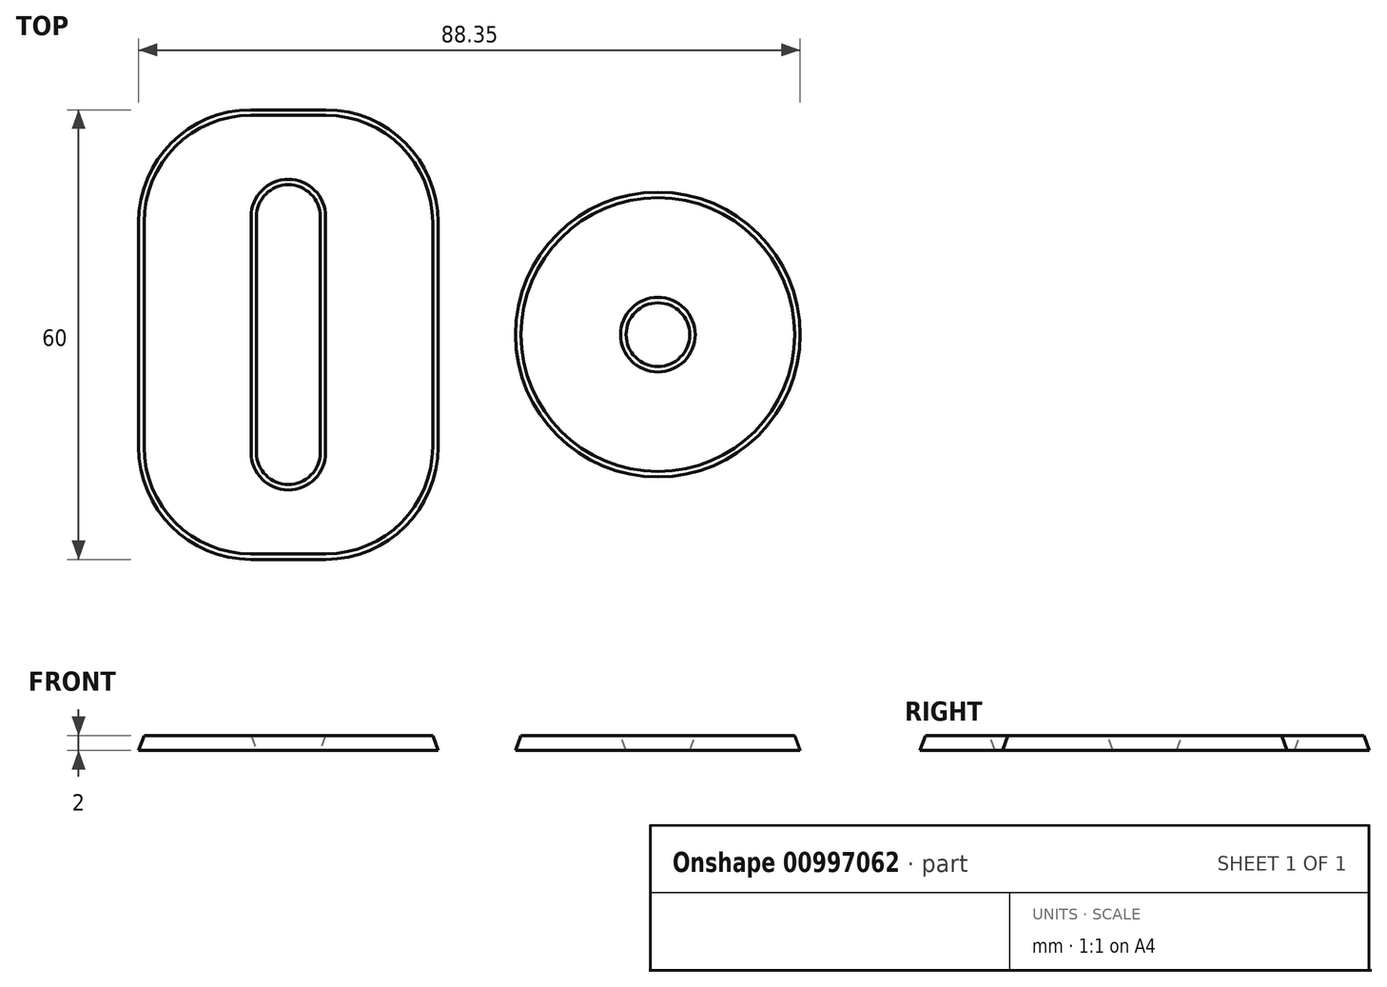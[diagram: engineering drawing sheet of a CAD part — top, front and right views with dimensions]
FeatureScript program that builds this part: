
annotation { "Feature Type Name" : "Feature", "Feature Type Description" : "" }
export const myFeature = defineFeature(function(context is Context, id is Id, definition is map)
    precondition{}
    {
        {
            var Q0;
            Q0=qCreatedBy(makeId("Top.planeOp"),FACE);
            var sketch = newSketch(context, id + "F0", { "sketchPlane" : qUnion([Q0])});
            skLineSegment(sketch, "E0.bottom", {"start": v(5, 30) * mm, "end": v(-5, 30) * mm});
            skLineSegment(sketch, "E0.top", {"start": v(5, -30) * mm, "end": v(-5, -30) * mm});
            skLineSegment(sketch, "E0.left", {"start": v(20, 15) * mm, "end": v(20, -15) * mm});
            skLineSegment(sketch, "E0.right", {"start": v(-20, 15) * mm, "end": v(-20, -15) * mm});
            skPoint(sketch, "E0.middle", {"position": v(0, 0) * mm});
            skPoint(sketch, "E1.visualSharp", {"position": v(-20, 30) * mm});
            skArc(sketch, "E1.filletArc", {"start": v(-5, 30) * mm, "mid": v(-15.6, 25.6) * mm, "end": v(-20, 15) * mm});
            skPoint(sketch, "E2.visualSharp", {"position": v(-20, -30) * mm});
            skArc(sketch, "E2.filletArc", {"start": v(-20, -15) * mm, "mid": v(-15.6, -25.6) * mm, "end": v(-5, -30) * mm});
            skPoint(sketch, "E3.visualSharp", {"position": v(20, -30) * mm});
            skArc(sketch, "E3.filletArc", {"start": v(5, -30) * mm, "mid": v(15.6, -25.6) * mm, "end": v(20, -15) * mm});
            skPoint(sketch, "E4.visualSharp", {"position": v(20, 30) * mm});
            skArc(sketch, "E4.filletArc", {"start": v(20, 15) * mm, "mid": v(15.6, 25.6) * mm, "end": v(5, 30) * mm});
            skLineSegment(sketch, "E5.bottom", {"start": v(4.25, 15.75) * mm, "end": v(-4.25, 15.75) * mm});
            skLineSegment(sketch, "E5.top", {"start": v(4.25, -15.75) * mm, "end": v(-4.25, -15.75) * mm});
            skLineSegment(sketch, "E5.left", {"start": v(4.25, 15.75) * mm, "end": v(4.25, -15.75) * mm});
            skLineSegment(sketch, "E5.right", {"start": v(-4.25, 15.75) * mm, "end": v(-4.25, -15.75) * mm});
            skCircle(sketch, "E6", {"center": v(0, 15.75) * mm, "radius": 4.25 * mm});
            skCircle(sketch, "E7", {"center": v(0, -15.75) * mm, "radius": 4.25 * mm});
            skLineSegment(sketch, "E8", {"start": v(0, 20) * mm, "end": v(0, -20) * mm, "construction": true});
            skCircle(sketch, "E9", {"center": v(49.35, 0) * mm, "radius": 19 * mm});
            skCircle(sketch, "E10", {"center": v(49.35, 0) * mm, "radius": 4.25 * mm});
            skSolve(sketch);
        }
        {
            var Q0;
            Q0=makeQuery(id+"F0.imprint","IMPRINT",FACE,{"disambiguationData":[TD([[makeQuery(id+"F0.imprint","IMPRINT",EDGE,{"derivedFrom":sQuery(id+"F0.wireOp",EDGE,"E0.bottom")}),1.0]])]});
            extrude(context, id + "F1", {"entities" : qUnion([Q0]), "depth" : 2 * mm, "offsetDistance" : 25 * mm, "hasDraft" : true, "draftAngle" : 20 * degree, "draftPullDirection" : true});
        }
        {
            var Q0;
            Q0=makeQuery(id+"F0.imprint","IMPRINT",FACE,{"disambiguationData":[TD([[makeQuery(id+"F0.imprint","IMPRINT",EDGE,{"derivedFrom":sQuery(id+"F0.wireOp",EDGE,"E9")}),1.0]])]});
            extrude(context, id + "F2", {"entities" : qUnion([Q0]), "depth" : 2 * mm, "offsetDistance" : 25 * mm, "hasDraft" : true, "draftAngle" : 20 * degree, "draftPullDirection" : true});
        }
    });
